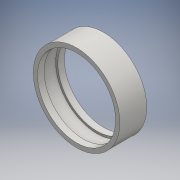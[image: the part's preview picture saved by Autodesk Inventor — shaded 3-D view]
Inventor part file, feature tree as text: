
AUTODESK INVENTOR PART (.ipt)
format: ipt  version: 2016 (Build 200138000, 138)  size: 168,448 bytes
history: native  units: mm
features: extrude x3, sketch x3
ambient origin geometry x8: Origin, YZ Plane, XZ Plane, XY Plane, X Axis, Y Axis, Z Axis, Center Point
bodies: Body1 (feature_tree)
feature tree (6):
  extrude  "Extrusion2"  Depth=40.592635mm
  extrude  "Extrusion3"  TaperAngle=0.0deg  [1 undecoded]
  extrude  "Extrusion4"  Depth=3.1mm
  sketch  "Sketch1"  dims[d0=38.592635mm d7=40.592635mm]
  sketch  "Sketch2"  dims[d10=12.59mm d11=0.0mm]
  sketch  "Sketch3"  dims[d12=38.592635mm d13=36.592635mm d14=3.1mm d15=0.0mm d16=38.592635mm d17=36.592635mm d18=3.1mm d19=0.0mm]
note: 1 required parameter value undecoded (feature->parameter linkage not recoverable at this tier; creation-order binding heuristic only, values carry confidence <= 0.55)
